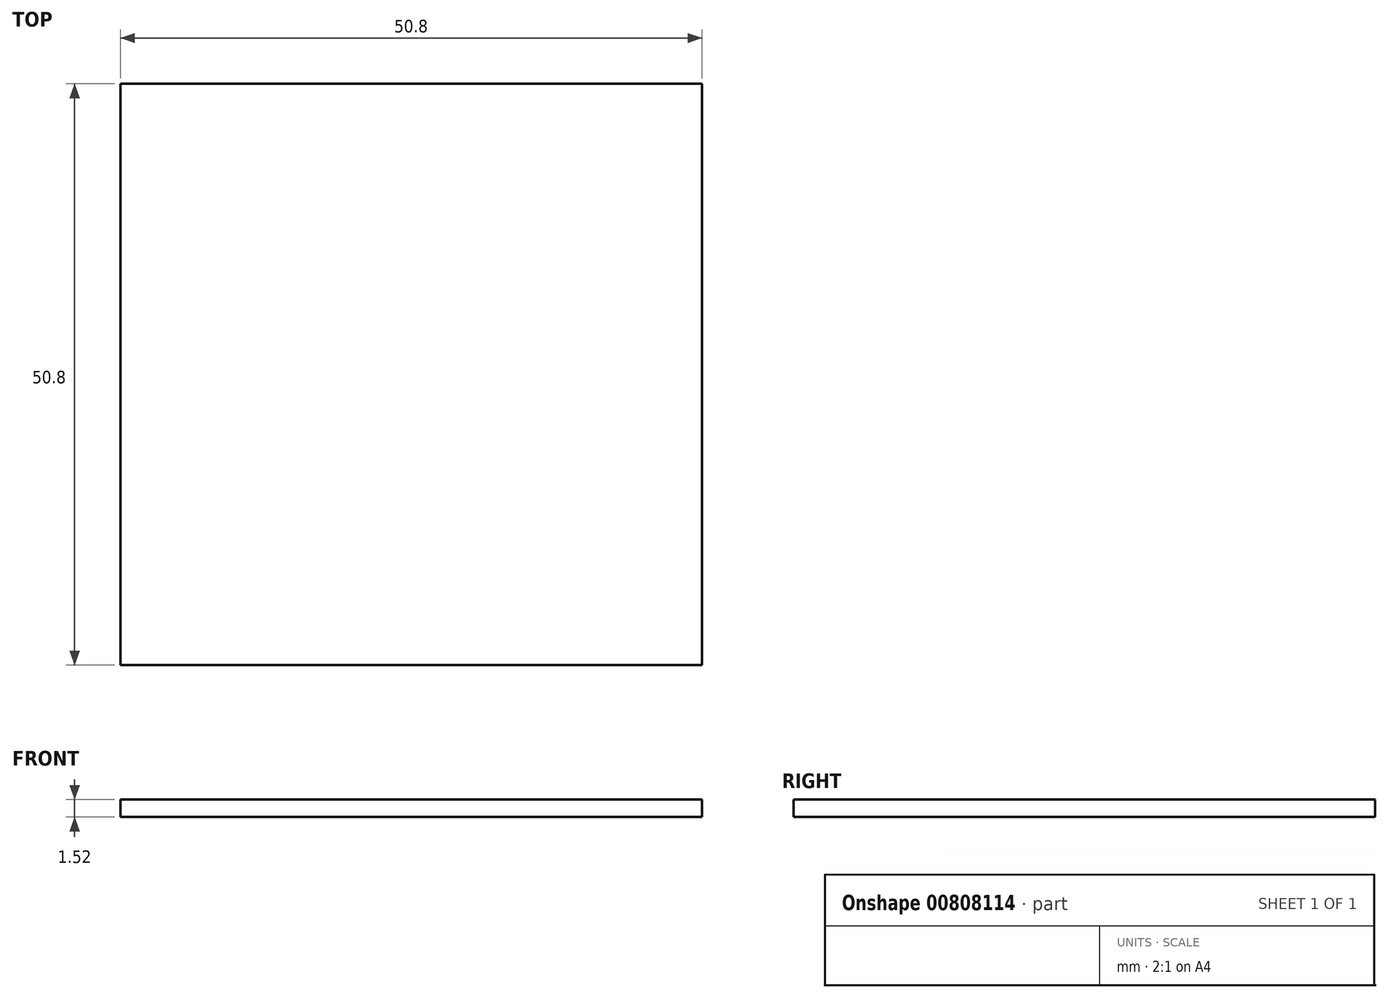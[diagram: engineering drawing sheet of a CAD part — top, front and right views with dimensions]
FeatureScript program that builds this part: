
annotation { "Feature Type Name" : "Feature", "Feature Type Description" : "" }
export const myFeature = defineFeature(function(context is Context, id is Id, definition is map)
    precondition{}
    {
        {
            var Q0;
            Q0=qCreatedBy(makeId("Top.planeOp"),FACE);
            var sketch = newSketch(context, id + "F0", { "sketchPlane" : qUnion([Q0])});
            skLineSegment(sketch, "E0.bottom", {"start": v(25.4, 25.4) * mm, "end": v(-25.4, 25.4) * mm});
            skLineSegment(sketch, "E0.top", {"start": v(25.4, -25.4) * mm, "end": v(-25.4, -25.4) * mm});
            skLineSegment(sketch, "E0.left", {"start": v(25.4, 25.4) * mm, "end": v(25.4, -25.4) * mm});
            skLineSegment(sketch, "E0.right", {"start": v(-25.4, 25.4) * mm, "end": v(-25.4, -25.4) * mm});
            skPoint(sketch, "E0.middle", {"position": v(0, 0) * mm});
            skSolve(sketch);
        }
        {
            var Q0;
            Q0=qSketchRegion(id+"F0",true);
            extrude(context, id + "F1", {"entities" : qUnion([Q0]), "endBound" : BoundingType.SYMMETRIC, "depth" : 1.52 * mm, "offsetDistance" : 25.4 * mm});
        }
    });
